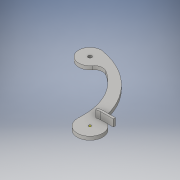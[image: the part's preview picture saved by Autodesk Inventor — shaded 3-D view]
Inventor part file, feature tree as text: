
AUTODESK INVENTOR PART (.ipt)
format: ipt  version: 2016 (Build 200138000, 138)  size: 168,448 bytes
history: native  units: in
note: dims shown in document units (in); Inventor stores cm internally (conversion verified against a paired STEP export)
features: sketch x16, other x3
ambient origin geometry x8: Origin, YZ Plane, XZ Plane, XY Plane, X Axis, Y Axis, Z Axis, Center Point
bodies: Solid1 (feature_tree)
feature tree (19):
  other  "Part3.ipt"
  other  "Solid1::Part3.ipt"
  other  "TaggingFeature1"
  sketch  "Sketch1"  dims[d0=0.3937in]
  sketch  "Sketch2"
  sketch  "Sketch3"
  sketch  "Sketch6"
  sketch  "Sketch7"
  sketch  "Sketch8"
  sketch  "Sketch9"
  sketch  "Sketch13"
  sketch  "Sketch14"
  sketch  "Sketch15"
  sketch  "Sketch16"
  sketch  "Sketch17"
  sketch  "Sketch18"
  sketch  "Sketch19"
  sketch  "Sketch20"
  sketch  "Sketch21"
